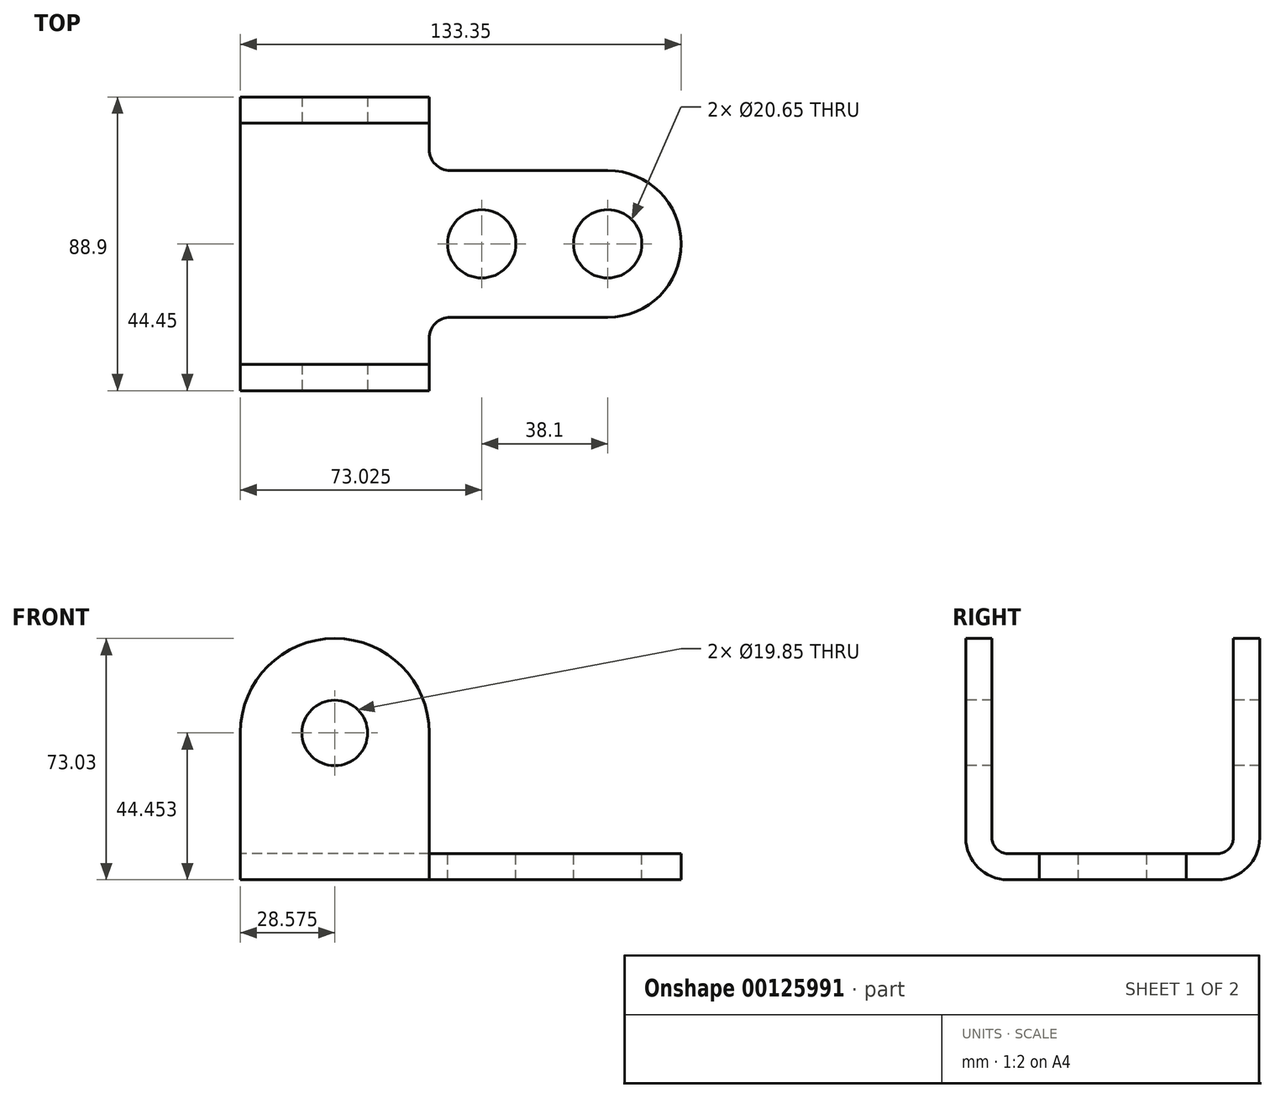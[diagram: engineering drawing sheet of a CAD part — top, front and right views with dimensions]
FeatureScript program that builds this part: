
annotation { "Feature Type Name" : "Feature", "Feature Type Description" : "" }
export const myFeature = defineFeature(function(context is Context, id is Id, definition is map)
    precondition{}
    {
        {
            var Q0;
            Q0=qCreatedBy(makeId("Right.planeOp"),FACE);
            var sketch = newSketch(context, id + "F0", { "sketchPlane" : qUnion([Q0])});
            skLineSegment(sketch, "E0", {"start": v(0, 0) * mm, "end": v(31.75, 0) * mm});
            skLineSegment(sketch, "E1", {"start": v(36.51, 4.76) * mm, "end": v(36.51, 65.09) * mm});
            skLineSegment(sketch, "E2", {"start": v(36.51, 65.09) * mm, "end": v(44.45, 65.09) * mm});
            skLineSegment(sketch, "E3", {"start": v(44.45, 65.09) * mm, "end": v(44.45, 4.76) * mm});
            skLineSegment(sketch, "E4", {"start": v(31.75, -7.94) * mm, "end": v(0, -7.94) * mm});
            skArc(sketch, "E5", {"start": v(31.75, 0) * mm, "mid": v(35.12, 1.4) * mm, "end": v(36.51, 4.76) * mm});
            skArc(sketch, "E6", {"start": v(31.75, -7.94) * mm, "mid": v(40.73, -4.22) * mm, "end": v(44.45, 4.76) * mm});
            skLineSegment(sketch, "E7.MirrorCS", {"start": v(-36.51, 65.09) * mm, "end": v(-44.45, 65.09) * mm});
            skLineSegment(sketch, "E8.MirrorCS", {"start": v(-36.51, 4.76) * mm, "end": v(-36.51, 65.09) * mm});
            skLineSegment(sketch, "E9.MirrorCS", {"start": v(-44.45, 65.09) * mm, "end": v(-44.45, 4.76) * mm});
            skArc(sketch, "E10.MirrorCS", {"start": v(-31.75, -7.94) * mm, "mid": v(-40.73, -4.22) * mm, "end": v(-44.45, 4.76) * mm});
            skArc(sketch, "E11.MirrorCS", {"start": v(-31.75, 0) * mm, "mid": v(-35.12, 1.4) * mm, "end": v(-36.51, 4.76) * mm});
            skLineSegment(sketch, "E12.MirrorCS", {"start": v(-31.75, -7.94) * mm, "end": v(0, -7.94) * mm});
            skLineSegment(sketch, "E13.MirrorCS", {"start": v(0, 0) * mm, "end": v(-31.75, 0) * mm});
            skSolve(sketch);
        }
        {
            var Q0;
            Q0=makeQuery(id+"F0.imprint","IMPRINT",FACE,{"disambiguationData":[TD([[makeQuery(id+"F0.imprint","IMPRINT",EDGE,{"derivedFrom":sQuery(id+"F0.wireOp",EDGE,"E0")}),-1.0]])]});
            var Q1;
            Q1=sQuery(id+"F0.wireOp",EDGE,"E5");
            var Q2;
            Q2=sQuery(id+"F0.wireOp",EDGE,"E8.MirrorCS");
            var Q3;
            Q3=sQuery(id+"F0.wireOp",EDGE,"E4");
            var Q4;
            Q4=sQuery(id+"F0.wireOp",EDGE,"E9.MirrorCS");
            var Q5;
            Q5=sQuery(id+"F0.wireOp",EDGE,"E6");
            var Q6;
            Q6=sQuery(id+"F0.wireOp",EDGE,"E7.MirrorCS");
            var Q7;
            Q7=sQuery(id+"F0.wireOp",EDGE,"E3");
            var Q8;
            Q8=sQuery(id+"F0.wireOp",EDGE,"E10.MirrorCS");
            var Q9;
            Q9=sQuery(id+"F0.wireOp",EDGE,"E12.MirrorCS");
            var Q10;
            Q10=sQuery(id+"F0.wireOp",EDGE,"E2");
            var Q11;
            Q11=sQuery(id+"F0.wireOp",EDGE,"E11.MirrorCS");
            var Q12;
            Q12=sQuery(id+"F0.wireOp",EDGE,"E1");
            var Q13;
            Q13=sQuery(id+"F0.wireOp",EDGE,"E13.MirrorCS");
            var Q14;
            Q14=sQuery(id+"F0.wireOp",EDGE,"E0");
            extrude(context, id + "F1", {"entities" : qUnion([Q0]), "surfaceEntities" : qUnion([Q1, Q2, Q3, Q4, Q5, Q6, Q7, Q8, Q9, Q10, Q11, Q12, Q13, Q14]), "depth" : 57.15 * mm});
        }
        {
            var Q0;
            Q0=makeQuery(id+"F1.opExtrude","SWEPT_FACE",FACE,{"disambiguationData":[OSD([sQuery(id+"F0.wireOp",EDGE,"E9.MirrorCS")])]});
            var sketch = newSketch(context, id + "F2", { "sketchPlane" : qUnion([Q0])});
            skLineSegment(sketch, "E14", {"start": v(0, 65.09) * mm, "end": v(0, -7.94) * mm});
            skLineSegment(sketch, "E15", {"start": v(0, -7.94) * mm, "end": v(57.15, -7.94) * mm});
            skLineSegment(sketch, "E16", {"start": v(57.15, -7.94) * mm, "end": v(57.15, 65.09) * mm});
            skLineSegment(sketch, "E17", {"start": v(57.15, 65.09) * mm, "end": v(0, 65.09) * mm});
            skCircle(sketch, "E18", {"center": v(28.58, 36.51) * mm, "radius": 9.92 * mm});
            skLineSegment(sketch, "E19", {"start": v(28.58, 36.51) * mm, "end": v(0, 36.51) * mm, "construction": true});
            skLineSegment(sketch, "E20", {"start": v(28.58, 36.51) * mm, "end": v(57.15, 36.51) * mm, "construction": true});
            skArc(sketch, "E21", {"start": v(57.15, 36.51) * mm, "mid": v(28.57, 65.09) * mm, "end": v(0, 36.51) * mm});
            skSolve(sketch);
        }
        {
            var Q0;
            Q0=makeQuery(id+"F2.imprint","IMPRINT",FACE,{"disambiguationData":[TD([[makeQuery(id+"F2.imprint","IMPRINT",EDGE,{"derivedFrom":sQuery(id+"F2.wireOp",EDGE,"E18")}),1.0]])]});
            var Q1;
            {var subQ0=sQuery(id+"F2.wireOp",EDGE,"E17");var subQ1=sQuery(id+"F2.wireOp",EDGE,"E14");var subQ2=makeQuery(id+"F2.imprint","INTERSECT",VERTEX,{"derivedFrom":[subQ1,subQ0]});Q1=makeQuery(id+"F2.imprint","IMPRINT",FACE,{"disambiguationData":[TD([[makeQuery(id+"F2.imprint","IMPRINT",EDGE,{"disambiguationData":[TD([[subQ2,-1.0]])],"derivedFrom":subQ1}),1.0]])]});}
            var Q2;
            {var subQ0=sQuery(id+"F2.wireOp",EDGE,"E17");var subQ1=sQuery(id+"F2.wireOp",EDGE,"E16");var subQ2=makeQuery(id+"F2.imprint","INTERSECT",VERTEX,{"derivedFrom":[subQ1,subQ0]});Q2=makeQuery(id+"F2.imprint","IMPRINT",FACE,{"disambiguationData":[TD([[makeQuery(id+"F2.imprint","IMPRINT",EDGE,{"disambiguationData":[TD([[subQ2,-1.0]])],"derivedFrom":subQ1}),-1.0]])]});}
            extrude(context, id + "F3", {"entities" : qUnion([Q0, Q1, Q2]), "operationType" : NewBodyOperationType.REMOVE, "endBound" : BoundingType.THROUGH_ALL, "oppositeDirection" : true, "depth" : 25.4 * mm});
        }
        {
            var Q0;
            Q0=makeQuery(id+"F1.opExtrude","SWEPT_FACE",FACE,{"disambiguationData":[OSD([sQuery(id+"F0.wireOp",EDGE,"E0"),sQuery(id+"F0.wireOp",EDGE,"E13.MirrorCS")])]});
            var sketch = newSketch(context, id + "F4", { "sketchPlane" : qUnion([Q0])});
            skLineSegment(sketch, "E22", {"start": v(57.15, 44.45) * mm, "end": v(57.15, 28.57) * mm});
            skLineSegment(sketch, "E23", {"start": v(63.5, 22.22) * mm, "end": v(111.12, 22.22) * mm});
            skArc(sketch, "E24", {"start": v(57.15, 28.57) * mm, "mid": v(59, 24.08) * mm, "end": v(63.5, 22.22) * mm});
            skArc(sketch, "E25", {"start": v(111.12, -22.23) * mm, "mid": v(133.35, 0) * mm, "end": v(111.12, 22.22) * mm});
            skLineSegment(sketch, "E26", {"start": v(111.12, -22.23) * mm, "end": v(63.5, -22.23) * mm});
            skLineSegment(sketch, "E27", {"start": v(57.15, -44.45) * mm, "end": v(57.15, -28.57) * mm});
            skArc(sketch, "E28", {"start": v(63.5, -22.23) * mm, "mid": v(59, -24.08) * mm, "end": v(57.15, -28.57) * mm});
            skCircle(sketch, "E29", {"center": v(111.12, 0) * mm, "radius": 10.33 * mm});
            skCircle(sketch, "E30", {"center": v(73.03, 0) * mm, "radius": 10.33 * mm});
            skSolve(sketch);
        }
        {
            var Q0;
            Q0=makeQuery(id+"F4.imprint","IMPRINT",FACE,{"disambiguationData":[TD([[makeQuery(id+"F4.imprint","IMPRINT",EDGE,{"derivedFrom":sQuery(id+"F4.wireOp",EDGE,"E23")}),-1.0]])]});
            extrude(context, id + "F5", {"entities" : qUnion([Q0]), "operationType" : NewBodyOperationType.ADD, "oppositeDirection" : true, "depth" : 7.94 * mm});
        }
    });
